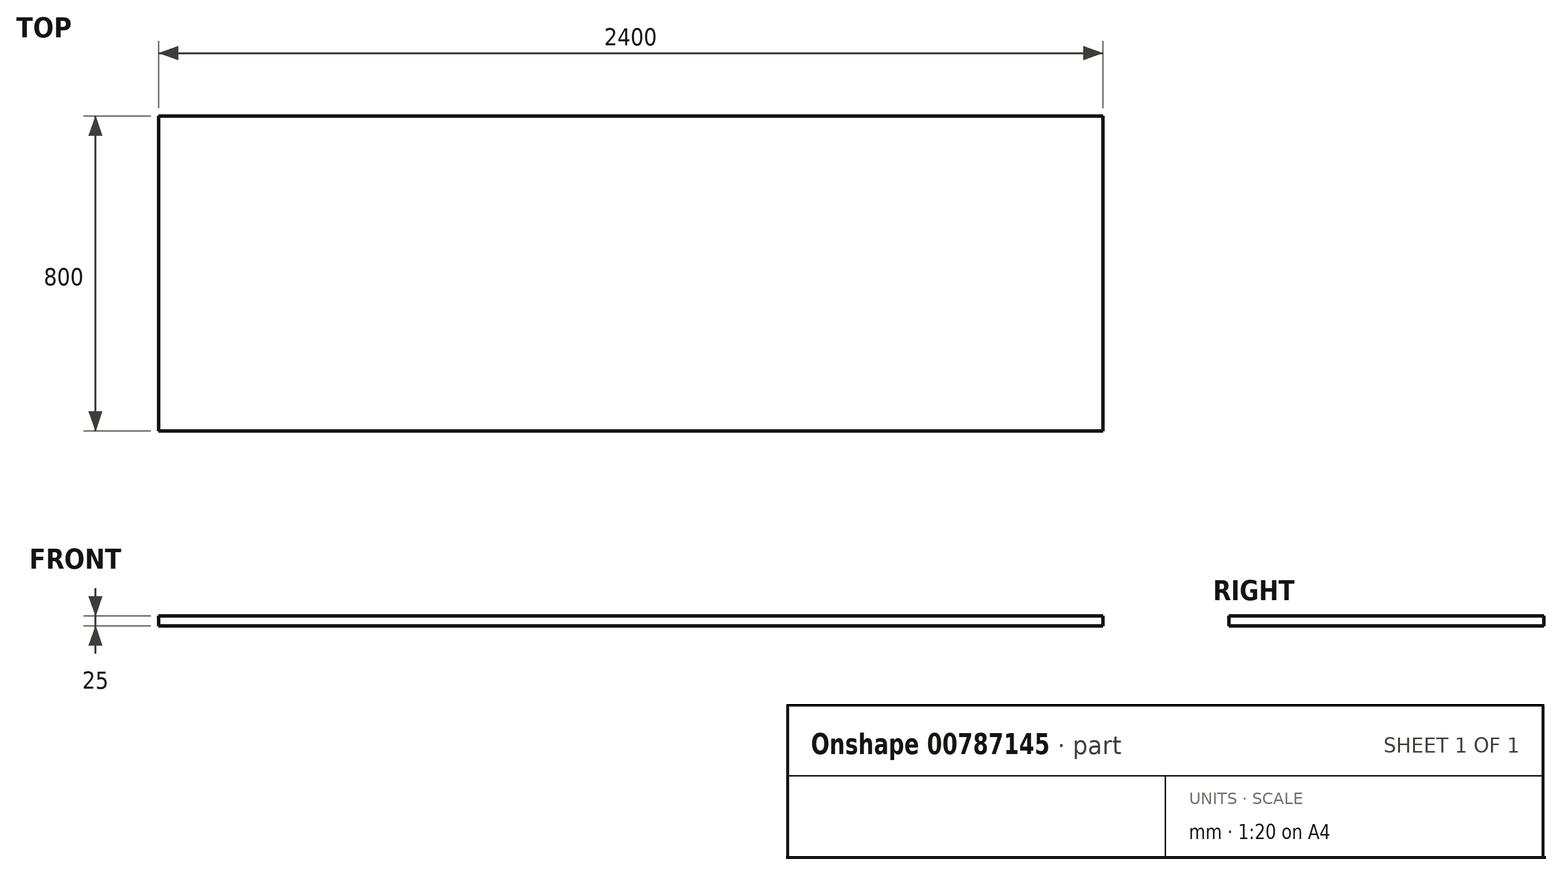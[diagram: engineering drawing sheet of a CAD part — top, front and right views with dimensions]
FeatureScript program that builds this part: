
annotation { "Feature Type Name" : "Feature", "Feature Type Description" : "" }
export const myFeature = defineFeature(function(context is Context, id is Id, definition is map)
    precondition{}
    {
        {
            var Q0;
            Q0=qCreatedBy(makeId("Top.planeOp"),FACE);
            var sketch = newSketch(context, id + "F0", { "sketchPlane" : qUnion([Q0])});
            skLineSegment(sketch, "E0.bottom", {"start": v(1128.36, -710.8) * mm, "end": v(-1271.64, -710.8) * mm});
            skLineSegment(sketch, "E0.top", {"start": v(1128.36, 89.2) * mm, "end": v(-1271.64, 89.2) * mm});
            skLineSegment(sketch, "E0.left", {"start": v(1128.36, -710.8) * mm, "end": v(1128.36, 89.2) * mm});
            skLineSegment(sketch, "E0.right", {"start": v(-1271.64, -710.8) * mm, "end": v(-1271.64, 89.2) * mm});
            skPoint(sketch, "E0.middle", {"position": v(-71.64, -310.8) * mm});
            skSolve(sketch);
        }
        {
            var Q0;
            Q0=makeQuery(id+"F0.imprint","IMPRINT",FACE,{"disambiguationData":[TD([[makeQuery(id+"F0.imprint","IMPRINT",EDGE,{"derivedFrom":sQuery(id+"F0.wireOp",EDGE,"E0.bottom")}),-1.0]])]});
            extrude(context, id + "F1", {"entities" : qUnion([Q0]), "depth" : 25 * mm, "offsetDistance" : 25 * mm});
        }
    });
